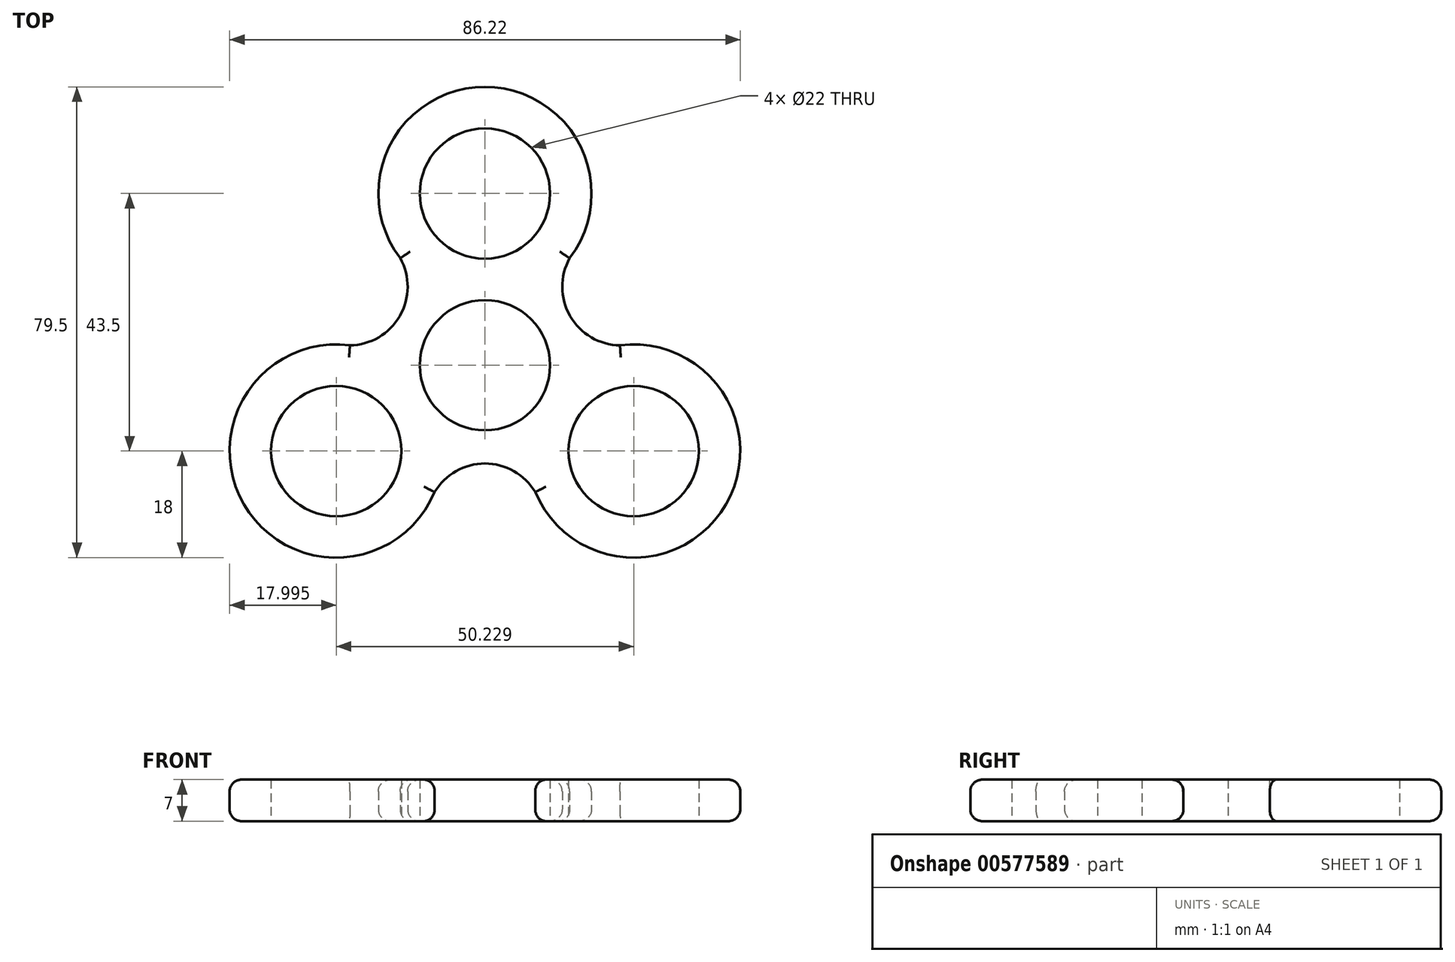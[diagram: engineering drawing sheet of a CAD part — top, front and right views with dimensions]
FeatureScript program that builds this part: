
annotation { "Feature Type Name" : "Feature", "Feature Type Description" : "" }
export const myFeature = defineFeature(function(context is Context, id is Id, definition is map)
    precondition{}
    {
        {
            var Q0;
            Q0=qCreatedBy(makeId("Top.planeOp"),FACE);
            var sketch = newSketch(context, id + "F0", { "sketchPlane" : qUnion([Q0])});
            skCircle(sketch, "E0", {"center": v(0, 0) * mm, "radius": 11 * mm});
            skLineSegment(sketch, "E1", {"start": v(0, 0) * mm, "end": v(0, 29) * mm});
            skCircle(sketch, "E2", {"center": v(0, 29) * mm, "radius": 11 * mm});
            skArc(sketch, "E3.0", {"start": v(14.3, 18.07) * mm, "mid": v(0, 47) * mm, "end": v(-14.3, 18.07) * mm});
            skCircle(sketch, "E4.1.0", {"center": v(-25.11, -14.5) * mm, "radius": 11 * mm});
            skArc(sketch, "E4.1.1", {"start": v(-22.8, 3.35) * mm, "mid": v(-40.7, -23.5) * mm, "end": v(-8.5, -21.42) * mm});
            skCircle(sketch, "E4.2.0", {"center": v(25.11, -14.5) * mm, "radius": 11 * mm});
            skArc(sketch, "E4.2.1", {"start": v(8.5, -21.42) * mm, "mid": v(40.7, -23.5) * mm, "end": v(22.8, 3.35) * mm});
            skArc(sketch, "E5", {"start": v(15.34, 19.58) * mm, "mid": v(14.38, 8.3) * mm, "end": v(24.63, 3.5) * mm});
            skArc(sketch, "E6.1.0", {"start": v(-24.63, 3.5) * mm, "mid": v(-14.38, 8.3) * mm, "end": v(-15.34, 19.58) * mm});
            skArc(sketch, "E6.2.0", {"start": v(9.29, -23.08) * mm, "mid": v(0, -16.6) * mm, "end": v(-9.29, -23.08) * mm});
            skSolve(sketch);
        }
        {
            var Q0;
            Q0 = qSketchRegion(id + "F0", true);
            extrude(context, id + "F1", {"entities" : qUnion([Q0]), "depth" : 7 * mm, "offsetDistance" : 25 * mm});
        }
        {
            var Q0;
            Q0=makeQuery(id+"F1.opExtrude","CAP_EDGE",EDGE,{"disambiguationData":[OSD([sQuery(id+"F0.wireOp",EDGE,"E6.1.0")])],"isStart":false});
            fillet(context, id + "F2", {"entities" : qUnion([Q0]), "radius" : 2 * mm, "tangentPropagation" : true, "allowEdgeOverflow" : false});
        }
        {
            var Q0;
            Q0=makeQuery(id+"F1.opExtrude","CAP_EDGE",EDGE,{"disambiguationData":[OSD([sQuery(id+"F0.wireOp",EDGE,"E4.1.1")])],"isStart":false});
            var Q1;
            Q1=makeQuery(id+"F1.opExtrude","CAP_EDGE",EDGE,{"disambiguationData":[OSD([sQuery(id+"F0.wireOp",EDGE,"E6.2.0")])],"isStart":false});
            var Q2;
            Q2=makeQuery(id+"F1.opExtrude","CAP_EDGE",EDGE,{"disambiguationData":[OSD([sQuery(id+"F0.wireOp",EDGE,"E4.2.1")])],"isStart":false});
            var Q3;
            Q3=makeQuery(id+"F1.opExtrude","CAP_EDGE",EDGE,{"disambiguationData":[OSD([sQuery(id+"F0.wireOp",EDGE,"E5")])],"isStart":false});
            var Q4;
            Q4=makeQuery(id+"F1.opExtrude","CAP_EDGE",EDGE,{"disambiguationData":[OSD([sQuery(id+"F0.wireOp",EDGE,"E3.0")])],"isStart":false});
            fillet(context, id + "F3", {"entities" : qUnion([Q0, Q1, Q2, Q3, Q4]), "radius" : 2 * mm, "tangentPropagation" : true, "allowEdgeOverflow" : false});
        }
        {
            var Q0;
            Q0=makeQuery(id+"F1.opExtrude","CAP_EDGE",EDGE,{"disambiguationData":[OSD([sQuery(id+"F0.wireOp",EDGE,"E4.2.1")])],"isStart":true});
            var Q1;
            Q1=makeQuery(id+"F1.opExtrude","CAP_EDGE",EDGE,{"disambiguationData":[OSD([sQuery(id+"F0.wireOp",EDGE,"E5")])],"isStart":true});
            var Q2;
            Q2=makeQuery(id+"F1.opExtrude","CAP_EDGE",EDGE,{"disambiguationData":[OSD([sQuery(id+"F0.wireOp",EDGE,"E3.0")])],"isStart":true});
            var Q3;
            Q3=makeQuery(id+"F1.opExtrude","CAP_EDGE",EDGE,{"disambiguationData":[OSD([sQuery(id+"F0.wireOp",EDGE,"E6.1.0")])],"isStart":true});
            var Q4;
            Q4=makeQuery(id+"F1.opExtrude","CAP_EDGE",EDGE,{"disambiguationData":[OSD([sQuery(id+"F0.wireOp",EDGE,"E4.1.1")])],"isStart":true});
            var Q5;
            Q5=makeQuery(id+"F1.opExtrude","CAP_EDGE",EDGE,{"disambiguationData":[OSD([sQuery(id+"F0.wireOp",EDGE,"E6.2.0")])],"isStart":true});
            fillet(context, id + "F4", {"entities" : qUnion([Q0, Q1, Q2, Q3, Q4, Q5]), "radius" : 2 * mm, "tangentPropagation" : true, "allowEdgeOverflow" : false});
        }
    });
